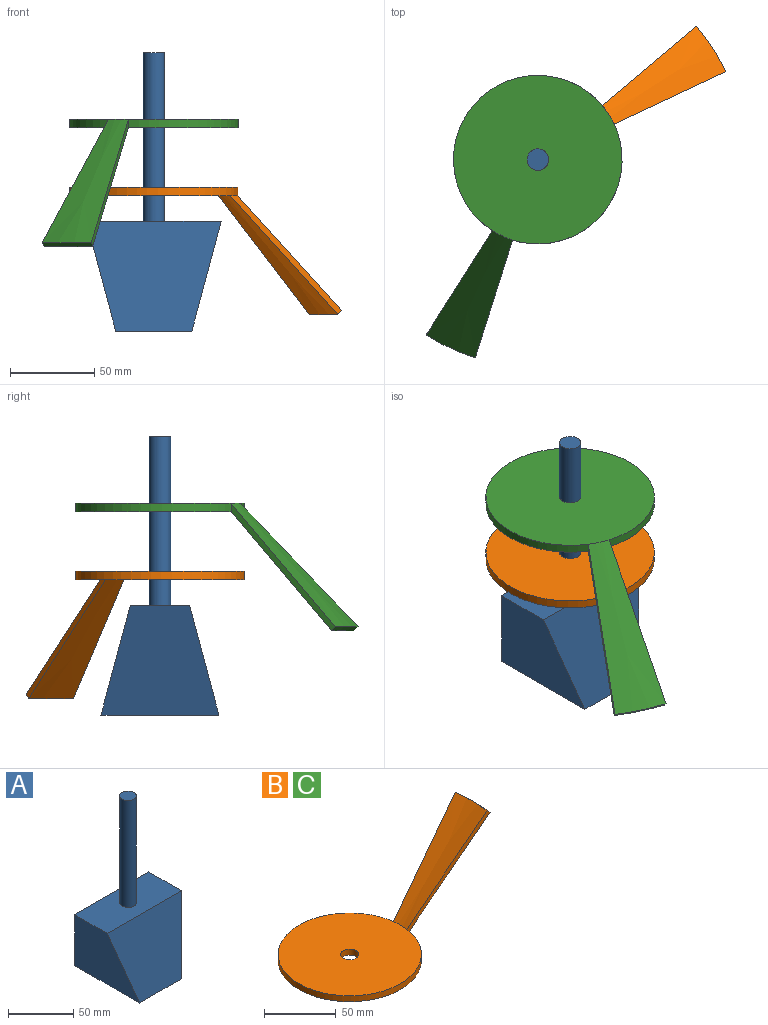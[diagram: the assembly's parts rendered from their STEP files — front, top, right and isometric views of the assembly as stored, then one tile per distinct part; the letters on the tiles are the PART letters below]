
ASSEMBLY  parts=3 mates=2
PART A: 8 faces, bbox 80x70x165 mm
  f0: plane 80x35.17mm, normal (0,0,1), area 2686.7mm2, adj f1,f2,f4,f5,f6
  f1: plane 70x65mm, normal (0.97,0,-0.26), area 3538.5mm2, adj f0,f3,f4,f5
  f2: plane 70x65mm, normal (-0.97,0,-0.26), area 3538.5mm2, adj f0,f3,f4,f5
  f3: plane 70x45.17mm, normal (0,0,-1), area 3161.7mm2, adj f1,f2,f4,f5
  f4: plane 80x65mm, normal (0,-0.97,0.26), area 4211.4mm2, adj f0,f1,f2,f3
  f5: plane 80x65mm, normal (0,0.97,0.26), area 4211.4mm2, adj f0,f1,f2,f3
  f6: cylinder r=6.35mm len=100mm, axis (0,0,-1), area 3989.8mm2, adj f0,f7
  f7: plane 12.7x12.7mm, normal (0,0,1), area 126.7mm2, adj f6
PART B: 9 faces, bbox 173.2x100x75.7 mm
  f0: cylinder r=50mm len=100mm, axis (0,0,-1), area 1505.3mm2, adj f2,f3,f7,f8
  f1: cylinder r=6.35mm len=12.7mm, axis (0,0,-1), area 199.5mm2, adj f2,f3
  f2: plane 100x100mm, normal (0,0,1), area 7727.3mm2, adj f0,f1,f5
  f3: plane 100x100mm, normal (0,0,-1), area 7727.3mm2, adj f0,f1,f6
  f4: cone r=123.21mm half-angle=45deg, axis (0,0,-1), area 112.9mm2, adj f5,f6,f7,f8
  f5: cone r=120.71mm half-angle=45deg, axis (0,0,1), area 2234.6mm2, adj f2,f4,f7,f8
  f6: cone r=50mm half-angle=45deg, axis (0,0,1), area 2347.5mm2, adj f3,f4,f7,f8
  f7: plane 75.71x72.58mm, normal (-0.13,0.99,0), area 359.8mm2, adj f0,f4,f5,f6
  f8: plane 75.71x72.58mm, normal (-0.13,-0.99,0), area 359.8mm2, adj f0,f4,f5,f6
PART C: same geometry as B
PLACE A t=(-941.85,565.22,-34.59)mm fixed
PLACE B rot(axis=(0.96,0.28,0),180deg) t=(-941.85,565.22,50.7)mm
PLACE C rot(axis=(0.54,-0.84,0),180deg) t=(-941.85,565.22,91.15)mm
MATE cylindrical B.f0 <-> A.f6  axis (0,0,-1) through (-941.85,565.22,45.7)mm
MATE cylindrical C.f0 <-> A.f6  axis (0,0,1) through (-941.85,565.22,91.15)mm
